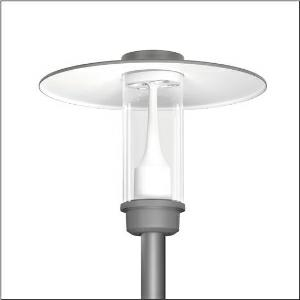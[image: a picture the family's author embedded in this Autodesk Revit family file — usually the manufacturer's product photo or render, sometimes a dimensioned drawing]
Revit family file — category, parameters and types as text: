
# Revit family: litepole_2_iq___pl1_2s_5xa5425cf14h_8640
name_source: partatom
category: Lighting Fixtures
units: mm (PartAtom-declared; Revit-internal decimal feet)

## family parameters
Cut with Voids When Loaded = No
Host = Face
Light Source = No
Part Type = Normal
Room Calculation Point = No
Round Connector Dimension = Use Diameter
Shared = No

## types (1)
- --- (1 x LED, 2990 lm, 23.9 W, 2200K)
    Apparent Load = 24 VA
    CIE Flux Codes = 22 60 92 98 100
    Color Rendering = 70
    Color Temperature = 2200K
    Default Elevation = 1800 mm
    Description = Litepole 2 iQ, mast luminaire, Module 540 iQ-SR, primary light control with 3 zone facetted reflector, of plastic, silver coated, highly specular, structured, primary optical cover: cover, of PMMA, transparent, light distribution: PL1.2s, light emission: direct distribution, primary light characteristic: symmetric, installation type: post-top, LED, High Power LED, rated luminous flux: 2.990lm, luminous efficacy: 125lm/W, light colour: 722, colour temperature: 2200K, control gear: iQ Street-Remote, control: pre-setting: logarithmic dimming characteristic, Street-Remote, Auto-Match, Temp-Guard, Lumen-Switch, Night-Set, Smart-Wire, Light-Fading, Desk-Remote (wireless, voltage-free reading and setting of iQ features in the workshop via application-optimized NFC function/RFID function), optimised constant luminous flux control (CLO 2.0), with terminal, 6-pole, max. 2.5mm², mains connection: 230..240V, AC, 50/60Hz, start of lifetime: 24W, end of service life: 26W, reduction: 12W, luminaire housing, upper part, of aluminium, coated, Siteco® metallic grey (DB 702S), diameter: 750mm, height: 590mm, spigot size: d x l = 76 x 70mm (post-top) | with reducer (optional accessory) 60 x 70mm, mounting height: 3..5m, post-top mast mounting element, of diecast aluminium, coated, Siteco® metallic grey (DB 702S), Module 540 iQ-SR, traffic white (RAL 9016), equipment: standard, protection rating (complete): IP65, insulation class (complete): insulation class II (safety insulation), certification: CE, ENEC, VDE, packaging unit: 1 piece

Light Distribution: PL1.2s
    Height = 590 mm
    Lamp = 1 x LED
    Lamp Light Flux = 2990 lm
    Lamp Power = 23.9 W
    Lamp count = 1
    Length = 750 mm
    Luminous efficacy = 125 lm/W
    Manufacturer = Siteco
    ModVariant = No
    Model = 5XA5425CF14H
    Number of Poles = 1
    OnlyDefault = Yes
    Power Factor = 1
    Product Name = Litepole 2 iQ | PL1.2s
    Product group = mast luminaire | pylon top
    ProductGroupID = 6100
    Protection Class = Protection class II
    Protection Degree = IP 65
    RLX_Detail_Level = 1
    RLX_Emergency_Light_Flux = 0 lm
    RLX_Emergency_Type = 0
    RLX_Emergency_Type_DB = No
    RlxData = <blob elided: 29481 chars, md5=9dbcfa1d>
    Socket = socket
    Standby Power = 0 W
    System Light Flux = 2990 lm
    System Power = 24 W
    Type Comments = factory setting: luminous flux: 100 % | dim-lin: 254 | 499 mA
    Type Image = l_1006518.jpg
    URL = http://relux.com
    VarID = @adj_144682
    Voltage = 0 V
    Weight = 0.00 kg
    Width = 0 mm  [stored 0 ft]

note: [stored X ft] marks values corroborated as IEEE doubles in the binary element streams (Revit-internal decimal feet)

## geometry (parser evidence)
native form markers: Blend x4, Sweep x10
no freeform markers — native parametric forms only
